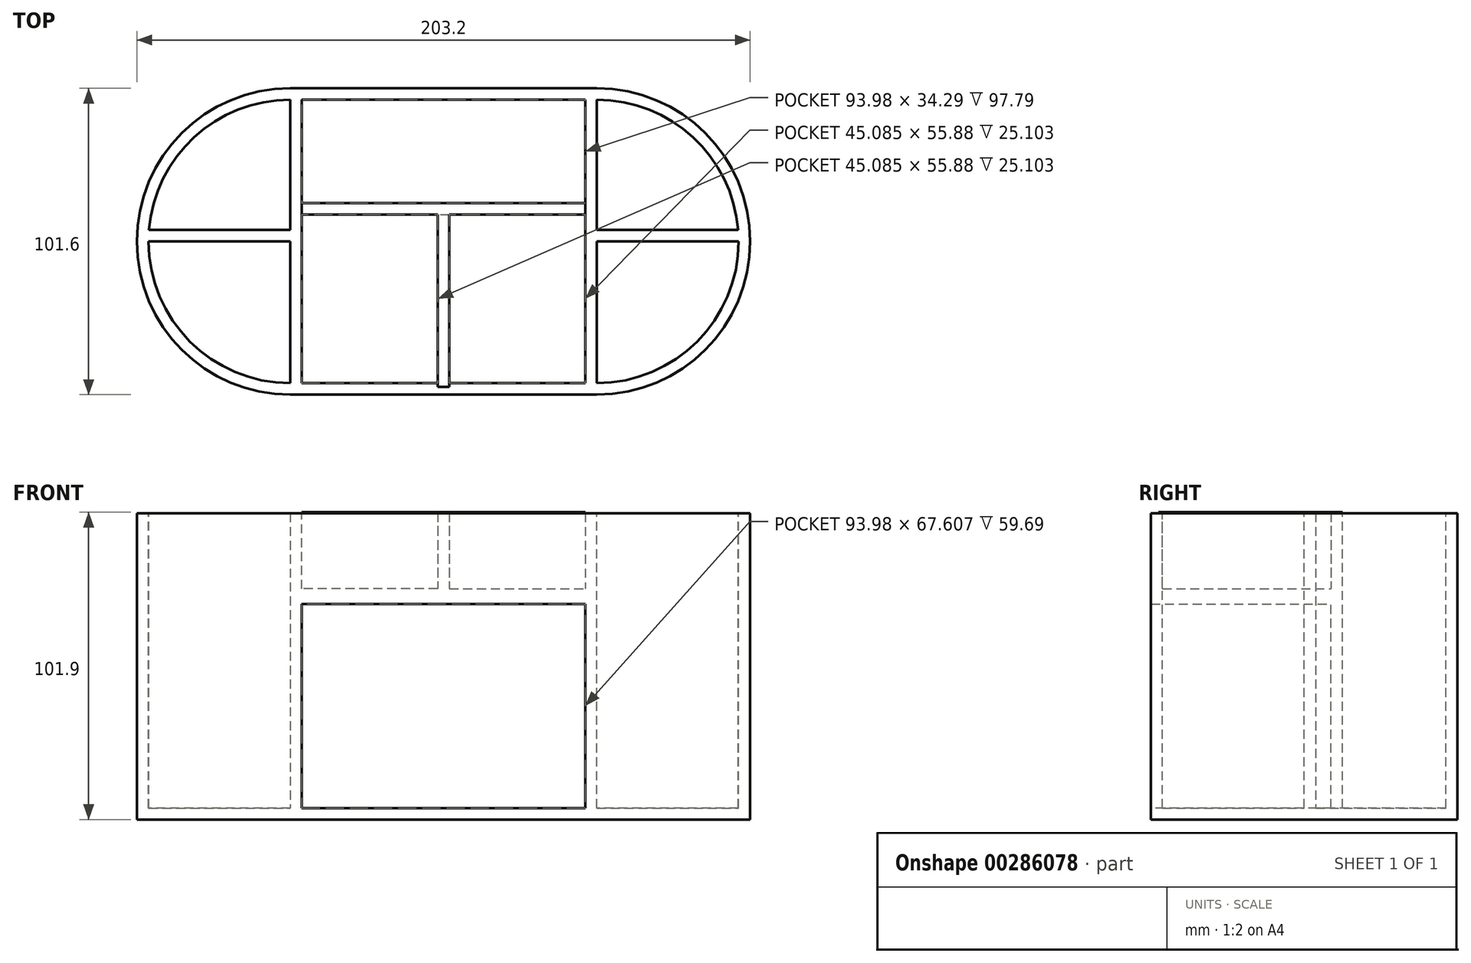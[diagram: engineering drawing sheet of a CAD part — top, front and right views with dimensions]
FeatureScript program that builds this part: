
annotation { "Feature Type Name" : "Feature", "Feature Type Description" : "" }
export const myFeature = defineFeature(function(context is Context, id is Id, definition is map)
    precondition{}
    {
        {
            var Q0;
            Q0=qCreatedBy(makeId("Top.planeOp"),FACE);
            var sketch = newSketch(context, id + "F0", { "sketchPlane" : qUnion([Q0])});
            skLineSegment(sketch, "E0.bottom", {"start": v(0, 0) * mm, "end": v(50.8, 0) * mm});
            skLineSegment(sketch, "E0.top", {"start": v(0, -101.6) * mm, "end": v(50.8, -101.6) * mm});
            skLineSegment(sketch, "E0.left", {"start": v(0, 0) * mm, "end": v(0, -101.6) * mm});
            skLineSegment(sketch, "E0.right", {"start": v(50.8, 0) * mm, "end": v(50.8, -101.6) * mm});
            skSolve(sketch);
        }
        {
            var Q0;
            Q0=makeQuery(id+"F0.imprint","IMPRINT",FACE,{"disambiguationData":[TD([[makeQuery(id+"F0.imprint","IMPRINT",EDGE,{"derivedFrom":sQuery(id+"F0.wireOp",EDGE,"E0.bottom")}),-1.0]])]});
            extrude(context, id + "F1", {"entities" : qUnion([Q0]), "depth" : 101.6 * mm});
        }
        {
            var Q0;
            Q0=makeQuery(id+"F1.opExtrude","CAP_FACE",FACE,{"disambiguationData":[OSD([sQuery(id+"F0.wireOp",EDGE,"E0.bottom"),sQuery(id+"F0.wireOp",EDGE,"E0.top"),sQuery(id+"F0.wireOp",EDGE,"E0.left"),sQuery(id+"F0.wireOp",EDGE,"E0.right")])],"isStart":false});
            var sketch = newSketch(context, id + "F2", { "sketchPlane" : qUnion([Q0])});
            skArc(sketch, "E1", {"start": v(50.8, -101.6) * mm, "mid": v(101.6, -50.8) * mm, "end": v(50.8, 0) * mm});
            skSolve(sketch);
        }
        {
            var Q0;
            Q0=makeQuery(id+"F2.imprint","IMPRINT",FACE,{"disambiguationData":[TD([[makeQuery(id+"F2.imprint","IMPRINT",EDGE,{"derivedFrom":sQuery(id+"F2.wireOp",EDGE,"E1")}),1.0]])]});
            var sketch = newSketch(context, id + "F3", { "sketchPlane" : qUnion([Q0])});
            skArc(sketch, "E2", {"start": v(50.9, -97.54) * mm, "mid": v(98.27, -49.98) * mm, "end": v(50.87, -2.45) * mm});
            skSolve(sketch);
        }
        {
            var Q0;
            Q0=makeQuery(id+"F2.imprint","IMPRINT",FACE,{"disambiguationData":[TD([[makeQuery(id+"F2.imprint","IMPRINT",EDGE,{"derivedFrom":sQuery(id+"F2.wireOp",EDGE,"E1")}),1.0]])]});
            extrude(context, id + "F4", {"entities" : qUnion([Q0]), "operationType" : NewBodyOperationType.ADD, "oppositeDirection" : true, "depth" : 101.6 * mm});
        }
        {
            var Q0;
            {var subQ0=sQuery(id+"F0.wireOp",EDGE,"E0.right");Q0=makeQuery(id+"F4.boolean.opBoolean","MERGE",FACE,{"derivedFrom":[makeQuery(id+"F1.opExtrude","CAP_FACE",FACE,{"disambiguationData":[OSD([sQuery(id+"F0.wireOp",EDGE,"E0.bottom"),sQuery(id+"F0.wireOp",EDGE,"E0.top"),sQuery(id+"F0.wireOp",EDGE,"E0.left"),subQ0])],"isStart":false}),makeQuery(id+"F4.opExtrude","CAP_FACE",FACE,{"disambiguationData":[OSD([subQ0,sQuery(id+"F2.wireOp",EDGE,"E1")])],"isStart":true})]});}
            shell(context, id + "F5", {"entities" : qUnion([Q0]), "thickness" : 3.8 * mm});
        }
        {
            var Q0;
            Q0=makeQuery(id+"F1.opExtrude","SWEPT_FACE",FACE,{"disambiguationData":[OSD([sQuery(id+"F0.wireOp",EDGE,"E0.top")])]});
            var sketch = newSketch(context, id + "F6", { "sketchPlane" : qUnion([Q0])});
            skLineSegment(sketch, "E3.bottom", {"start": v(50.8, 101.6) * mm, "end": v(47, 101.6) * mm});
            skLineSegment(sketch, "E3.top", {"start": v(50.8, 0) * mm, "end": v(47, 0) * mm});
            skLineSegment(sketch, "E3.left", {"start": v(50.8, 101.6) * mm, "end": v(50.8, 0) * mm});
            skLineSegment(sketch, "E3.right", {"start": v(47, 101.6) * mm, "end": v(47, 0) * mm});
            skSolve(sketch);
        }
        {
            var Q0;
            Q0=makeQuery(id+"F6.imprint","IMPRINT",FACE,{"disambiguationData":[TD([[makeQuery(id+"F6.imprint","IMPRINT",EDGE,{"derivedFrom":sQuery(id+"F6.wireOp",EDGE,"E3.bottom")}),-1.0]])]});
            extrude(context, id + "F7", {"entities" : qUnion([Q0]), "operationType" : NewBodyOperationType.ADD, "oppositeDirection" : true, "depth" : 101.6 * mm});
        }
        {
            var Q0;
            Q0=makeQuery(id+"F5.opShell","OFFSET_FACE",FACE,{"disambiguationData":[OSD([sQuery(id+"F0.wireOp",EDGE,"E0.left")])]});
            extrude(context, id + "F8", {"entities" : qUnion([Q0]), "operationType" : NewBodyOperationType.REMOVE, "oppositeDirection" : true, "depth" : 25.4 * mm});
        }
        {
            var Q0;
            Q0=makeQuery(id+"F1.opExtrude","SWEPT_FACE",FACE,{"disambiguationData":[OSD([sQuery(id+"F0.wireOp",EDGE,"E0.top")])]});
            var sketch = newSketch(context, id + "F9", { "sketchPlane" : qUnion([Q0])});
            skLineSegment(sketch, "E4.bottom", {"start": v(50.8, 76.5) * mm, "end": v(0, 76.5) * mm});
            skLineSegment(sketch, "E4.top", {"start": v(50.8, 71.42) * mm, "end": v(0, 71.42) * mm});
            skLineSegment(sketch, "E4.left", {"start": v(50.8, 76.5) * mm, "end": v(50.8, 71.42) * mm});
            skLineSegment(sketch, "E4.right", {"start": v(0, 76.5) * mm, "end": v(0, 71.42) * mm});
            skSolve(sketch);
        }
        {
            var Q0;
            Q0=makeQuery(id+"F9.imprint","IMPRINT",FACE,{"disambiguationData":[TD([[makeQuery(id+"F9.imprint","IMPRINT",EDGE,{"derivedFrom":sQuery(id+"F9.wireOp",EDGE,"E4.bottom")}),1.0]])]});
            extrude(context, id + "F10", {"entities" : qUnion([Q0]), "operationType" : NewBodyOperationType.ADD, "oppositeDirection" : true, "depth" : 63.5 * mm});
        }
        {
            var Q0;
            Q0=makeQuery(id+"F10.opExtrude","SWEPT_FACE",FACE,{"disambiguationData":[OSD([sQuery(id+"F9.wireOp",EDGE,"E4.bottom")])]});
            var sketch = newSketch(context, id + "F11", { "sketchPlane" : qUnion([Q0])});
            skLineSegment(sketch, "E5.bottom", {"start": v(0, -38.1) * mm, "end": v(47, -38.1) * mm});
            skLineSegment(sketch, "E5.top", {"start": v(0, -41.91) * mm, "end": v(47, -41.91) * mm});
            skLineSegment(sketch, "E5.left", {"start": v(0, -38.1) * mm, "end": v(0, -41.91) * mm});
            skLineSegment(sketch, "E5.right", {"start": v(47, -38.1) * mm, "end": v(47, -41.91) * mm});
            skSolve(sketch);
        }
        {
            var Q0;
            Q0=makeQuery(id+"F11.imprint","IMPRINT",FACE,{"disambiguationData":[TD([[makeQuery(id+"F11.imprint","IMPRINT",EDGE,{"derivedFrom":sQuery(id+"F11.wireOp",EDGE,"E5.bottom")}),1.0]])]});
            extrude(context, id + "F12", {"entities" : qUnion([Q0]), "operationType" : NewBodyOperationType.ADD, "depth" : 25.4 * mm});
        }
        {
            var Q0;
            Q0=makeQuery(id+"F12.opExtrude","CAP_FACE",FACE,{"disambiguationData":[OSD([sQuery(id+"F11.wireOp",EDGE,"E5.bottom"),sQuery(id+"F11.wireOp",EDGE,"E5.top"),sQuery(id+"F11.wireOp",EDGE,"E5.left"),sQuery(id+"F11.wireOp",EDGE,"E5.right")])],"isStart":false});
            extrude(context, id + "F13", {"entities" : qUnion([Q0]), "operationType" : NewBodyOperationType.ADD, "oppositeDirection" : true, "depth" : 101.6 * mm});
        }
        {
            var Q0;
            {var subQ0=sQuery(id+"F0.wireOp",EDGE,"E0.left");var subQ1=sQuery(id+"F0.wireOp",EDGE,"E0.top");Q0=makeQuery(id+"F10.boolean.opBoolean","SPLIT",FACE,{"disambiguationData":[TD([makeQuery(id+"F10.opExtrude","SWEPT_FACE",FACE,{"disambiguationData":[OSD([sQuery(id+"F9.wireOp",EDGE,"E4.top")])]})])],"derivedFrom":makeQuery(id+"F8.boolean.opBoolean","MERGE",FACE,{"derivedFrom":[makeQuery(id+"F5.opShell","OFFSET_FACE",FACE,{"disambiguationData":[OSD([subQ1])]}),makeQuery(id+"F8.opExtrude","SWEPT_FACE",FACE,{"disambiguationData":[OSD([subQ1,subQ0])]})]})});}
            extrude(context, id + "F14", {"entities" : qUnion([Q0]), "operationType" : NewBodyOperationType.REMOVE, "oppositeDirection" : true, "depth" : 25.4 * mm});
        }
        {
            var Q0;
            Q0=makeQuery(id+"F12.opExtrude","SWEPT_FACE",FACE,{"disambiguationData":[OSD([sQuery(id+"F11.wireOp",EDGE,"E5.top")])]});
            var sketch = newSketch(context, id + "F15", { "sketchPlane" : qUnion([Q0])});
            skLineSegment(sketch, "E6.bottom", {"start": v(0, 101.9) * mm, "end": v(1.9, 101.9) * mm});
            skLineSegment(sketch, "E6.top", {"start": v(0, 76.5) * mm, "end": v(1.9, 76.5) * mm});
            skLineSegment(sketch, "E6.left", {"start": v(0, 101.9) * mm, "end": v(0, 76.5) * mm});
            skLineSegment(sketch, "E6.right", {"start": v(1.9, 101.9) * mm, "end": v(1.9, 76.5) * mm});
            skSolve(sketch);
        }
        {
            var Q0;
            Q0=makeQuery(id+"F15.imprint","IMPRINT",FACE,{"disambiguationData":[TD([[makeQuery(id+"F15.imprint","IMPRINT",EDGE,{"derivedFrom":sQuery(id+"F15.wireOp",EDGE,"E6.bottom")}),-1.0]])]});
            extrude(context, id + "F16", {"entities" : qUnion([Q0]), "operationType" : NewBodyOperationType.ADD, "depth" : 57.15 * mm});
        }
        {
            var Q0;
            Q0=makeQuery(id+"F1.opExtrude","SWEPT_BODY",BODY,{"disambiguationData":[OSD([sQuery(id+"F0.wireOp",EDGE,"E0.bottom"),sQuery(id+"F0.wireOp",EDGE,"E0.top"),sQuery(id+"F0.wireOp",EDGE,"E0.left"),sQuery(id+"F0.wireOp",EDGE,"E0.right")])]});
            var Q1;
            Q1=qCreatedBy(makeId("Right.planeOp"),FACE);
            mirror(context, id + "F17", {"operationType" : NewBodyOperationType.ADD, "entities" : qUnion([Q0]), "mirrorPlane" : qUnion([Q1])});
        }
        {
            var Q0;
            Q0=makeQuery(id+"F17.opPattern","COPY",FACE,{"derivedFrom":makeQuery(id+"F7.opExtrude","SWEPT_FACE",FACE,{"disambiguationData":[OSD([sQuery(id+"F6.wireOp",EDGE,"E3.left")])]}),"instanceName":"1"});
            var sketch = newSketch(context, id + "F18", { "sketchPlane" : qUnion([Q0])});
            skLineSegment(sketch, "E7.bottom", {"start": v(47, 101.6) * mm, "end": v(50.8, 101.6) * mm});
            skLineSegment(sketch, "E7.top", {"start": v(47, 3.81) * mm, "end": v(50.8, 3.81) * mm});
            skLineSegment(sketch, "E7.left", {"start": v(47, 101.6) * mm, "end": v(47, 3.81) * mm});
            skLineSegment(sketch, "E7.right", {"start": v(50.8, 101.6) * mm, "end": v(50.8, 3.81) * mm});
            skSolve(sketch);
        }
        {
            var Q0;
            Q0=makeQuery(id+"F18.imprint","IMPRINT",FACE,{"disambiguationData":[TD([[makeQuery(id+"F18.imprint","IMPRINT",EDGE,{"derivedFrom":sQuery(id+"F18.wireOp",EDGE,"E7.bottom")}),-1.0]])]});
            extrude(context, id + "F19", {"entities" : qUnion([Q0]), "operationType" : NewBodyOperationType.ADD, "depth" : 49.53 * mm});
        }
        {
            var Q0;
            Q0=makeQuery(id+"F1.opExtrude","SWEPT_BODY",BODY,{"disambiguationData":[OSD([sQuery(id+"F0.wireOp",EDGE,"E0.bottom"),sQuery(id+"F0.wireOp",EDGE,"E0.top"),sQuery(id+"F0.wireOp",EDGE,"E0.left"),sQuery(id+"F0.wireOp",EDGE,"E0.right")])]});
            var Q1;
            Q1=qCreatedBy(makeId("Right.planeOp"),FACE);
            mirror(context, id + "F20", {"operationType" : NewBodyOperationType.ADD, "entities" : qUnion([Q0]), "mirrorPlane" : qUnion([Q1])});
        }
    });
